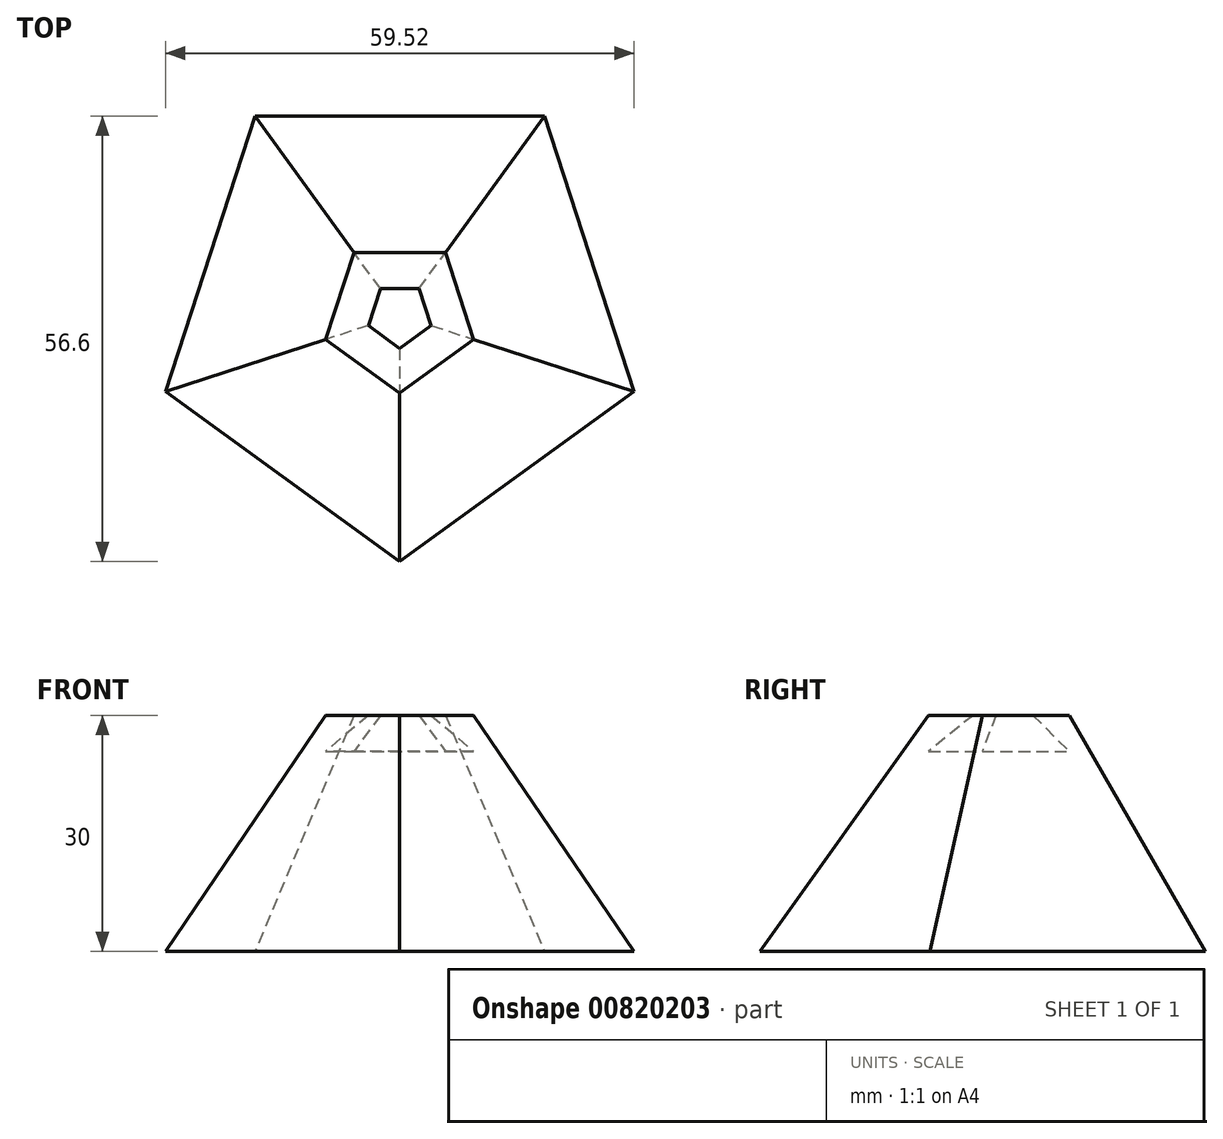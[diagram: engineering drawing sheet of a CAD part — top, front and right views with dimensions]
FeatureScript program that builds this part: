
annotation { "Feature Type Name" : "Feature", "Feature Type Description" : "" }
export const myFeature = defineFeature(function(context is Context, id is Id, definition is map)
    precondition{}
    {
        {
            var Q0;
            Q0=qCreatedBy(makeId("Top.planeOp"),FACE);
            var sketch = newSketch(context, id + "F0", { "sketchPlane" : qUnion([Q0])});
            skCircle(sketch, "E0.cCircle", {"center": v(0, 0) * mm, "radius": 25.31 * mm, "construction": true});
            skLineSegment(sketch, "E0.0", {"start": v(-18.4, 25.31) * mm, "end": v(18.4, 25.31) * mm});
            skLineSegment(sketch, "E0.1", {"start": v(18.4, 25.31) * mm, "end": v(29.76, -9.67) * mm});
            skLineSegment(sketch, "E0.2", {"start": v(29.76, -9.67) * mm, "end": v(0, -31.29) * mm});
            skLineSegment(sketch, "E0.3", {"start": v(0, -31.29) * mm, "end": v(-29.76, -9.67) * mm});
            skLineSegment(sketch, "E0.4", {"start": v(-29.76, -9.67) * mm, "end": v(-18.4, 25.31) * mm});
            skPoint(sketch, "E0.0.midPoint", {"position": v(0, 25.31) * mm});
            skSolve(sketch);
        }
        {
            var Q0;
            Q0 = qSketchRegion(id + "F0", true);
            extrude(context, id + "F1", {"entities" : qUnion([Q0]), "depth" : 30 * mm, "offsetDistance" : 25.4 * mm, "hasDraft" : true, "draftAngle" : 30 * degree, "draftPullDirection" : true});
        }
        {
            var Q0;
            Q0=qCreatedBy(makeId("Top.planeOp"),FACE);
            cPlane(context, id + "F2", {"entities" : qUnion([Q0]), "cplaneType" : CPlaneType.OFFSET, "offset" : 25.4 * mm, "width" : 152.4 * mm, "height" : 152.4 * mm});
        }
        {
            var Q0;
            Q0=qCreatedBy(id+"F2.planeOp",FACE);
            var sketch = newSketch(context, id + "F3", { "sketchPlane" : qUnion([Q0])});
            skLineSegment(sketch, "E1.0.0", {"start": v(-5.8, 8) * mm, "end": v(-9.4, -3.05) * mm});
            skLineSegment(sketch, "E1.0.1", {"start": v(-9.4, -3.05) * mm, "end": v(0, -9.88) * mm});
            skLineSegment(sketch, "E1.0.2", {"start": v(0, -9.88) * mm, "end": v(9.4, -3.05) * mm});
            skLineSegment(sketch, "E1.0.3", {"start": v(9.4, -3.05) * mm, "end": v(5.8, 8) * mm});
            skLineSegment(sketch, "E1.0.4", {"start": v(5.8, 8) * mm, "end": v(-5.8, 8) * mm});
            skSolve(sketch);
        }
        {
            var Q0;
            Q0 = qSketchRegion(id + "F3", true);
            extrude(context, id + "F4", {"entities" : qUnion([Q0]), "operationType" : NewBodyOperationType.REMOVE, "depth" : 30 * mm, "offsetDistance" : 25.4 * mm, "hasDraft" : true, "draftAngle" : 45 * degree, "draftPullDirection" : true});
        }
        {
            var Q0;
            Q0=qCreatedBy(id+"F2.planeOp",FACE);
            cPlane(context, id + "F5", {"entities" : qUnion([Q0]), "cplaneType" : CPlaneType.OFFSET, "offset" : 25.4 * mm, "width" : 152.4 * mm, "height" : 152.4 * mm});
        }
    });
